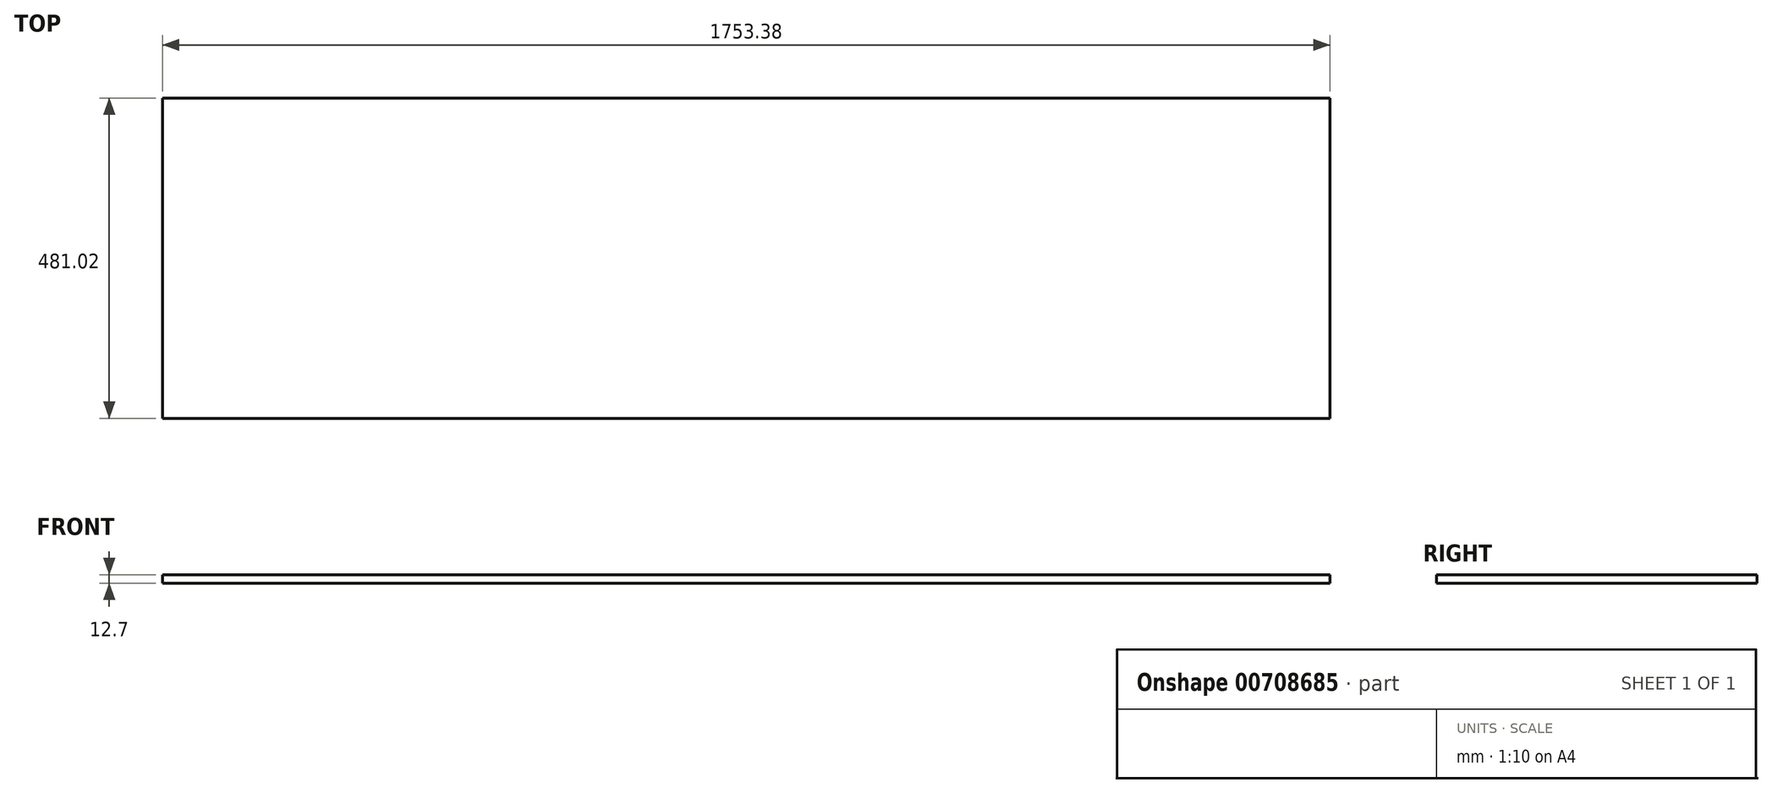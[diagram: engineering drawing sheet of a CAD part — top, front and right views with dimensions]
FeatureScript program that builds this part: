
annotation { "Feature Type Name" : "Feature", "Feature Type Description" : "" }
export const myFeature = defineFeature(function(context is Context, id is Id, definition is map)
    precondition{}
    {
        {
            var Q0;
            Q0=qCreatedBy(makeId("Top.planeOp"),FACE);
            var sketch = newSketch(context, id + "F0", { "sketchPlane" : qUnion([Q0])});
            skLineSegment(sketch, "E0.bottom", {"start": v(876.7, -240.5) * mm, "end": v(-876.7, -240.5) * mm});
            skLineSegment(sketch, "E0.top", {"start": v(876.7, 240.5) * mm, "end": v(-876.7, 240.5) * mm});
            skLineSegment(sketch, "E0.left", {"start": v(876.7, -240.5) * mm, "end": v(876.7, 240.5) * mm});
            skLineSegment(sketch, "E0.right", {"start": v(-876.7, -240.5) * mm, "end": v(-876.7, 240.5) * mm});
            skPoint(sketch, "E0.middle", {"position": v(0, 0) * mm});
            skSolve(sketch);
        }
        {
            var Q0;
            Q0=makeQuery(id+"F0.imprint","IMPRINT",FACE,{"disambiguationData":[TD([[makeQuery(id+"F0.imprint","IMPRINT",EDGE,{"derivedFrom":sQuery(id+"F0.wireOp",EDGE,"E0.bottom")}),-1.0]])]});
            extrude(context, id + "F1", {"entities" : qUnion([Q0]), "depth" : 12.7 * mm, "offsetDistance" : 25.4 * mm});
        }
    });
